# Revit family: IS_ConnectSpace_E0352_BIM_DE
name_source: partatom
category: Plumbing Fixtures
revit_build: Autodesk Revit MEP 2016 (Build: 20161004_0715(x64)
units: mm (PartAtom-declared; Revit-internal decimal feet)

## family parameters
Always vertical = No
Cut with Voids When Loaded = No
OmniClass Number = 23.45.05.14.17.11
OmniClass Title = Shower Compartments
Part Type = Normal
Room Calculation Point = No
Round Connector Dimension = Use Diameter
Shared = No
Work Plane-Based = No

## types (1)
- E035267 - CONNECT SPACE box for vanity unit 112x78mm
    Accessories = www.idealstandard.de\ersatzteile
    AssetType = Fixed
    BIMObjectName = ISI_IdealStandard_VanityUnits_ConnectSpace_E035267
    BIMobject category = Storage
    BOSUseNativeGeometries = 1
    BarCode = 5017830454892
    Brand = Ideal Standard
    Brand url = http://www.idealstandard.de
    CodePerformance = 0
    Color = NEUTRAL
    ConnectionType = Plumbing
    Cost = 0 $
    CurrencyUnit = €
    CurrentRevision = 1
    Date of publishing = 20/12/2017
    Description = IS Aufbewahrungsbox CONNECT SPACE, mit Deckel, 112x78x75mm, hellgrau
    DurationUnit = Year
    EAN code = https://5017830454892
    Edition number = 1
    ExpectedLife = 25
    Features = IS Aufbewahrungsbox CONNECT SPACE, mit Deckel, 112x78x75mm, hellgrau
    Finish = NEUTRAL
    IFC Classification = Sanitary Terminal
    IfcExportAs = IfcSanitaryTerminalType
    Installation instructions = http://www.idealstandard.de
    InstallationInstructions = www.idealstandard.de\produkte
    MainColor = NEUTRAL
    MaintenanceInformation = www.idealstandard.de\produkte
    Manufacturer name = Ideal Standard
    ManufacturerURL = http://www.idealstandard.de
    Material = 0
    Model = E035267
    ModelNumber = E035267
    ModelReference = IS Aufbewahrungsbox CONNECT SPACE, mit Deckel, 112x78x75mm, hellgrau
    NBS Reference Code = 35-75-94
    NBS Reference Description = Vanity Units
    Name = VanityUnits_ConnectSpace_E035267
    NettWeight = 0.15 Kg
    Nominal height = 75
    Nominal width = 112
    NominalDepth = 78 mm  [stored 0.255906 ft]
    NominalHeight = 79 mm
    NominalLength = 78 mm  [stored 0.255906 ft]
    NominalWidth = 112 mm  [stored 0.367454 ft]
    Product Guid = 5108446f-558c-4d2f-baf7-25f2d8792dc8
    Product SKU = E0352
    Product data url = https://bimobject.com
    Product family = Sanitary
    Product group = Furniture
    Product name = CONNECT SPACE box for vanity unit 112x78mm
    Product url = http://www.idealstandard.de
    ProductInformation = www.idealstandard.de/produkte
    QR code = http://bimobject.com
    Shape = Sculptured
    Size = 79 x 78 x 112mm
    Space = Internal
    SpareParts = www.idealstandard.de/ersatzteile
    Technical description = http://www.idealstandard.de
    URL = http://www.idealstandard.de
    Uniclass 2.0 Code = PR-35-75-94
    Uniclass 2.0 Description = Vanity Units
    Uniclass 2015 Code = Pr_40_20_76_94
    Uniclass 2015 Name = Vanity units
    Uniclass2015Code = Pr_40_20_76_94
    Uniclass2015Title = Vanity units
    Uniclass2015Version = Products v1.1
    Version = 1
    VolumeUnits = Litres
    Weight Net (Kg) = 0.15

note: [stored X ft] marks values corroborated as IEEE doubles in the binary element streams (Revit-internal decimal feet)

## geometry (parser evidence)
native form markers: Blend x4, Sweep x1
no freeform markers — native parametric forms only
